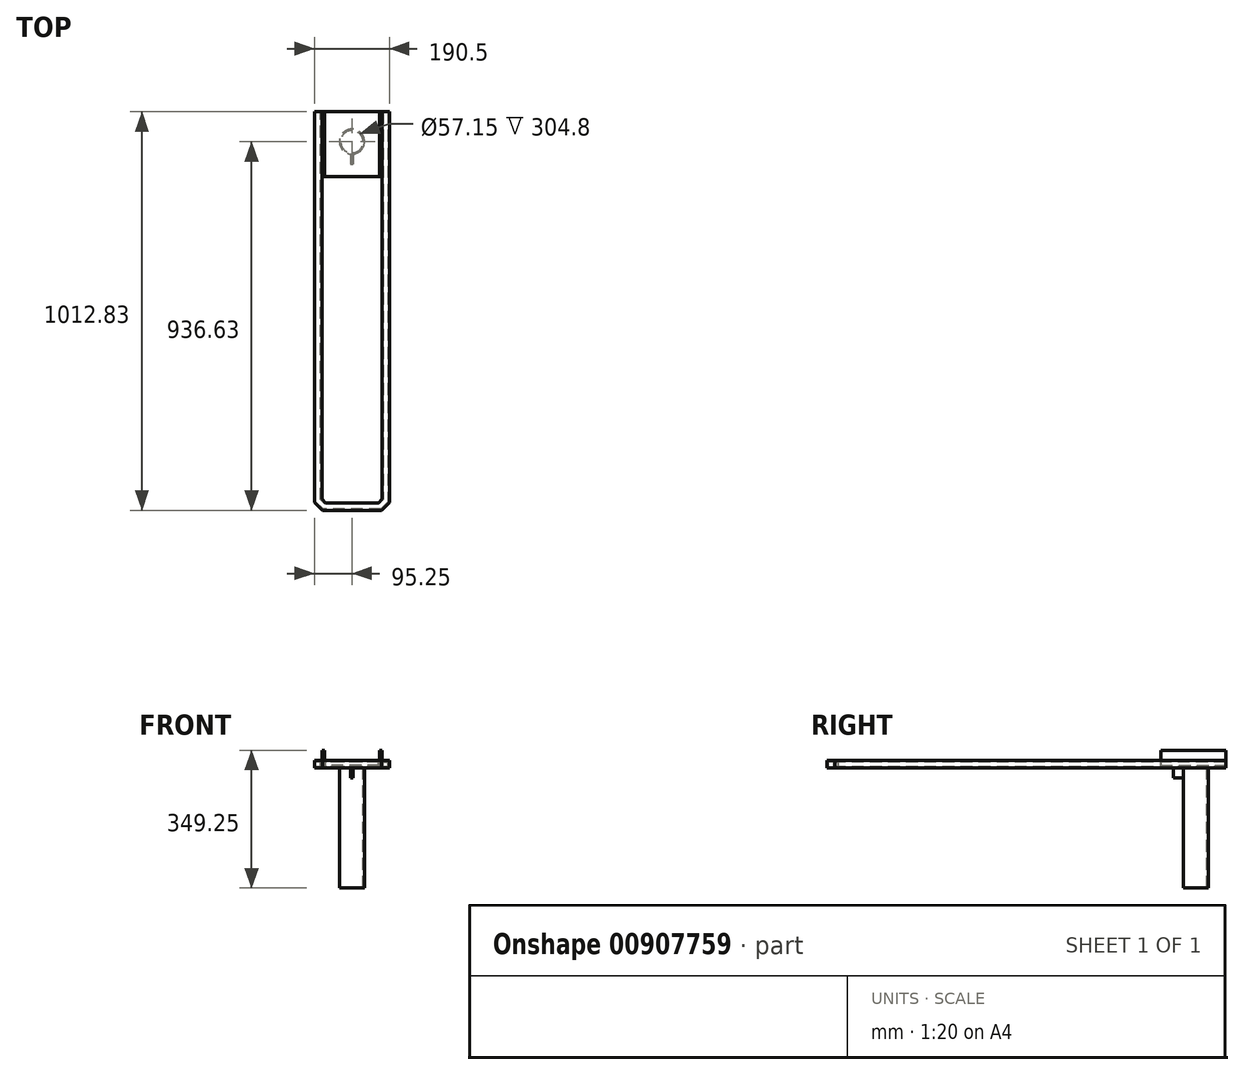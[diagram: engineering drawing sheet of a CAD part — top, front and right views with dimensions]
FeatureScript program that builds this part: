
annotation { "Feature Type Name" : "Feature", "Feature Type Description" : "" }
export const myFeature = defineFeature(function(context is Context, id is Id, definition is map)
    precondition{}
    {
        {
            var Q0;
            Q0=qCreatedBy(makeId("Top.planeOp"),FACE);
            var sketch = newSketch(context, id + "F0", { "sketchPlane" : qUnion([Q0])});
            skCircle(sketch, "E0", {"center": v(0, 0) * mm, "radius": 31.75 * mm});
            skCircle(sketch, "E1", {"center": v(0, 0) * mm, "radius": 28.57 * mm});
            skSolve(sketch);
        }
        {
            var Q0;
            Q0=makeQuery(id+"F0.imprint","IMPRINT",FACE,{"disambiguationData":[TD([[makeQuery(id+"F0.imprint","IMPRINT",EDGE,{"derivedFrom":sQuery(id+"F0.wireOp",EDGE,"E0")}),1.0]])]});
            extrude(context, id + "F1", {"entities" : qUnion([Q0]), "oppositeDirection" : true, "depth" : 304.8 * mm, "offsetDistance" : 25.4 * mm});
        }
        {
            var Q0;
            Q0=qCreatedBy(makeId("Top.planeOp"),FACE);
            var sketch = newSketch(context, id + "F2", { "sketchPlane" : qUnion([Q0])});
            skLineSegment(sketch, "E2.bottom", {"start": v(-3.18, -28.58) * mm, "end": v(3.18, -28.58) * mm});
            skLineSegment(sketch, "E2.top", {"start": v(-3.18, -57.15) * mm, "end": v(3.18, -57.15) * mm});
            skLineSegment(sketch, "E2.left", {"start": v(-3.18, -28.58) * mm, "end": v(-3.18, -57.15) * mm});
            skLineSegment(sketch, "E2.right", {"start": v(3.17, -28.58) * mm, "end": v(3.17, -57.15) * mm});
            skSolve(sketch);
        }
        {
            var Q0;
            Q0=makeQuery(id+"F2.imprint","IMPRINT",FACE,{"disambiguationData":[TD([[makeQuery(id+"F2.imprint","IMPRINT",EDGE,{"derivedFrom":sQuery(id+"F2.wireOp",EDGE,"E2.bottom")}),-1.0]])]});
            extrude(context, id + "F3", {"entities" : qUnion([Q0]), "operationType" : NewBodyOperationType.ADD, "oppositeDirection" : true, "depth" : 25.4 * mm, "offsetDistance" : 25.4 * mm});
        }
        {
            var Q0;
            Q0=qCreatedBy(makeId("Front.planeOp"),FACE);
            cPlane(context, id + "F4", {"entities" : qUnion([Q0]), "cplaneType" : CPlaneType.OFFSET, "offset" : 76.2 * mm, "oppositeDirection" : true, "width" : 152.4 * mm, "height" : 152.4 * mm});
        }
        {
            var Q0;
            Q0=qCreatedBy(id+"F4.planeOp",FACE);
            var sketch = newSketch(context, id + "F5", { "sketchPlane" : qUnion([Q0])});
            skLineSegment(sketch, "E3", {"start": v(76.2, 0) * mm, "end": v(76.2, 44.45) * mm});
            skLineSegment(sketch, "E4", {"start": v(69.85, 44.45) * mm, "end": v(69.85, 6.35) * mm});
            skLineSegment(sketch, "E5", {"start": v(69.85, 6.35) * mm, "end": v(-69.85, 6.35) * mm});
            skLineSegment(sketch, "E6", {"start": v(-69.85, 6.35) * mm, "end": v(-69.85, 44.45) * mm});
            skLineSegment(sketch, "E7", {"start": v(-76.2, 44.45) * mm, "end": v(-76.2, 0) * mm});
            skLineSegment(sketch, "E8", {"start": v(-76.2, 0) * mm, "end": v(76.2, 0) * mm});
            skLineSegment(sketch, "E9", {"start": v(-76.2, 44.45) * mm, "end": v(-69.85, 44.45) * mm});
            skLineSegment(sketch, "E10", {"start": v(69.85, 44.45) * mm, "end": v(76.2, 44.45) * mm});
            skSolve(sketch);
        }
        {
            var Q0;
            Q0=makeQuery(id+"F5.imprint","IMPRINT",FACE,{"disambiguationData":[TD([[makeQuery(id+"F5.imprint","IMPRINT",EDGE,{"derivedFrom":sQuery(id+"F5.wireOp",EDGE,"E3")}),1.0]])]});
            var Q1;
            Q1 = qSketchRegion(id + "F7", true);
            var Q2;
            Q2 = qSketchRegion(id + "F8", true);
            extrude(context, id + "F6", {"entities" : qUnion([Q0, Q1, Q2]), "operationType" : NewBodyOperationType.ADD, "depth" : 165.1 * mm, "offsetDistance" : 25.4 * mm});
        }
        {
            var Q0;
            Q0=qCreatedBy(id+"F4.planeOp",FACE);
            var sketch = newSketch(context, id + "F7", { "sketchPlane" : qUnion([Q0])});
            skLineSegment(sketch, "E11.bottom", {"start": v(76.2, 0) * mm, "end": v(95.25, 0) * mm});
            skLineSegment(sketch, "E11.top", {"start": v(76.2, 19.05) * mm, "end": v(95.25, 19.05) * mm});
            skLineSegment(sketch, "E11.left", {"start": v(76.2, 0) * mm, "end": v(76.2, 19.05) * mm});
            skLineSegment(sketch, "E11.right", {"start": v(95.25, 0) * mm, "end": v(95.25, 19.05) * mm});
            skLineSegment(sketch, "E12.bottom", {"start": v(79.38, 3.18) * mm, "end": v(92.08, 3.18) * mm});
            skLineSegment(sketch, "E12.top", {"start": v(79.38, 15.88) * mm, "end": v(92.08, 15.88) * mm});
            skLineSegment(sketch, "E12.left", {"start": v(79.38, 3.18) * mm, "end": v(79.38, 15.88) * mm});
            skLineSegment(sketch, "E12.right", {"start": v(92.08, 3.17) * mm, "end": v(92.08, 15.88) * mm});
            skSolve(sketch);
        }
        {
            var Q0;
            Q0=makeQuery(id+"F6.opExtrude","SWEPT_FACE",FACE,{"disambiguationData":[OSD([sQuery(id+"F5.wireOp",EDGE,"E5")])]});
            var sketch = newSketch(context, id + "F8", { "sketchPlane" : qUnion([Q0])});
            skLineSegment(sketch, "E13", {"start": v(98.42, 76.2) * mm, "end": v(98.43, -917.57) * mm});
            skLineSegment(sketch, "E14", {"start": v(-98.43, 76.2) * mm, "end": v(-98.42, -917.57) * mm});
            skLineSegment(sketch, "E15", {"start": v(-98.43, -917.57) * mm, "end": v(-76.2, -939.8) * mm});
            skLineSegment(sketch, "E16", {"start": v(-76.2, -939.8) * mm, "end": v(76.2, -939.8) * mm});
            skLineSegment(sketch, "E17", {"start": v(76.2, -939.8) * mm, "end": v(98.43, -917.57) * mm});
            skSolve(sketch);
        }
        {
            var Q0;
            Q0=makeQuery(id+"F7.imprint","IMPRINT",FACE,{"disambiguationData":[TD([[makeQuery(id+"F7.imprint","IMPRINT",EDGE,{"derivedFrom":sQuery(id+"F7.wireOp",EDGE,"E11.bottom")}),1.0]])]});
            var Q1;
            Q1=sQuery(id+"F8.wireOp",EDGE,"E13");
            var Q2;
            Q2=sQuery(id+"F8.wireOp",EDGE,"E17");
            var Q3;
            Q3=sQuery(id+"F8.wireOp",EDGE,"E16");
            var Q4;
            Q4=sQuery(id+"F8.wireOp",EDGE,"E15");
            var Q5;
            Q5=sQuery(id+"F8.wireOp",EDGE,"E14");
            sweep(context, id + "F9", {"operationType" : NewBodyOperationType.ADD, "profiles" : qUnion([Q0]), "path" : qUnion([Q1, Q2, Q3, Q4, Q5])});
        }
    });
